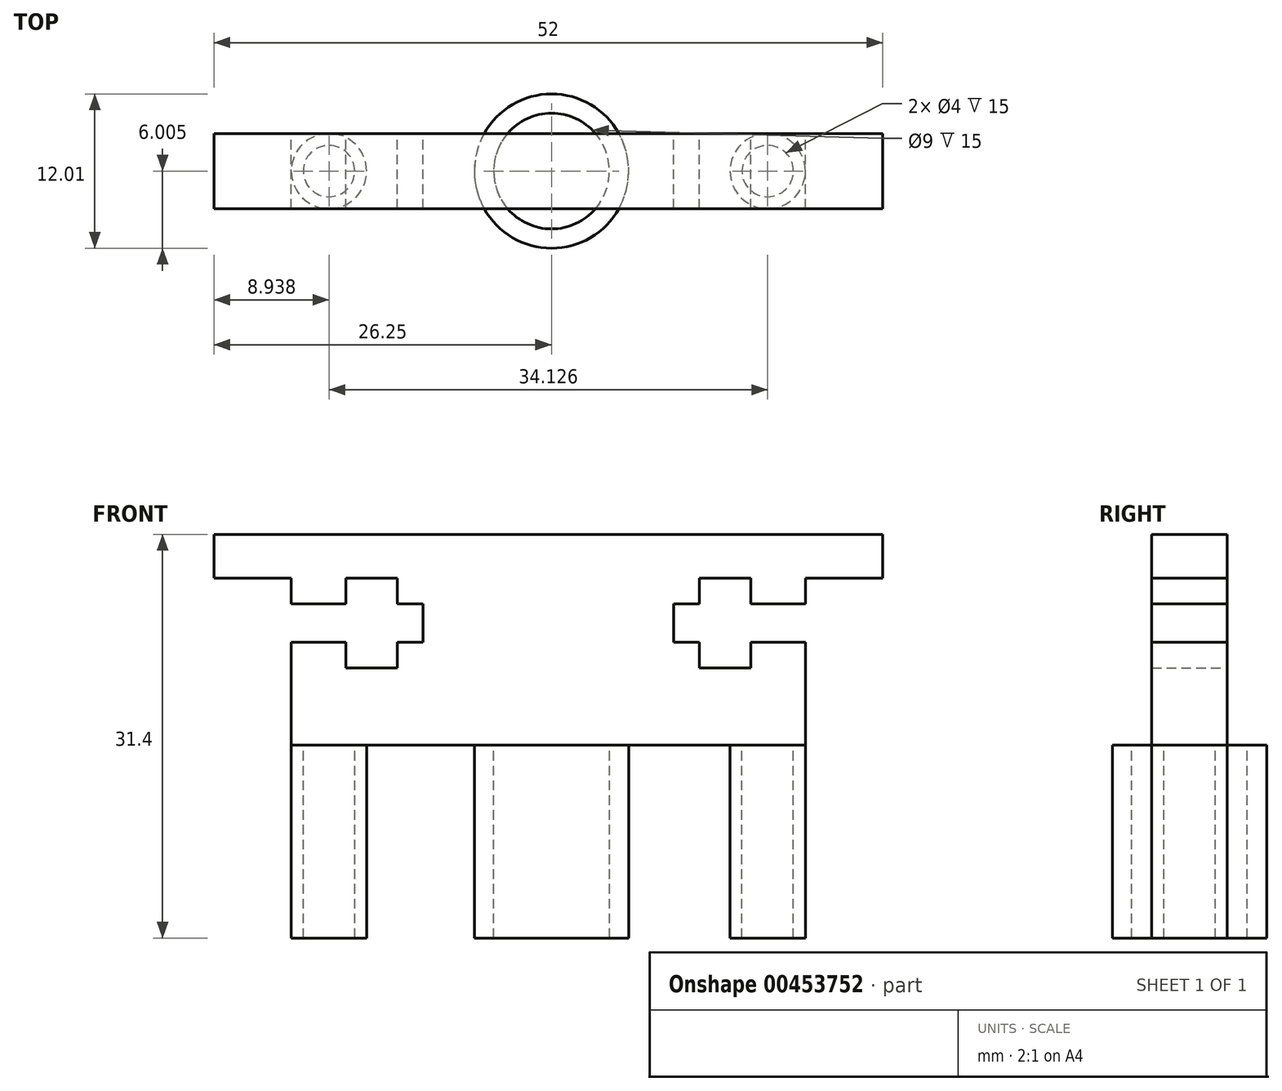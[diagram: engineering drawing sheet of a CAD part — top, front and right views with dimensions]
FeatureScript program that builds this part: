
annotation { "Feature Type Name" : "Feature", "Feature Type Description" : "" }
export const myFeature = defineFeature(function(context is Context, id is Id, definition is map)
    precondition{}
    {
        {
            var Q0;
            Q0=qCreatedBy(makeId("Front.planeOp"),FACE);
            var sketch = newSketch(context, id + "F0", { "sketchPlane" : qUnion([Q0])});
            skLineSegment(sketch, "E0", {"start": v(-19.23, 35.5) * mm, "end": v(-19.23, 32.1) * mm});
            skLineSegment(sketch, "E1", {"start": v(-13.23, 32.1) * mm, "end": v(-19.23, 32.1) * mm});
            skLineSegment(sketch, "E2", {"start": v(-13.23, 32.1) * mm, "end": v(-13.23, 30.1) * mm});
            skLineSegment(sketch, "E3", {"start": v(-13.23, 30.1) * mm, "end": v(-8.98, 30.1) * mm});
            skLineSegment(sketch, "E4", {"start": v(-8.98, 30.1) * mm, "end": v(-8.98, 32.1) * mm});
            skLineSegment(sketch, "E5", {"start": v(-8.98, 32.1) * mm, "end": v(-4.98, 32.1) * mm});
            skLineSegment(sketch, "E6", {"start": v(-4.98, 32.1) * mm, "end": v(-4.98, 30.1) * mm});
            skLineSegment(sketch, "E7", {"start": v(-4.98, 30.1) * mm, "end": v(-2.98, 30.1) * mm});
            skLineSegment(sketch, "E8", {"start": v(-2.98, 30.1) * mm, "end": v(-2.98, 27.1) * mm});
            skLineSegment(sketch, "E9", {"start": v(-2.98, 27.1) * mm, "end": v(-4.98, 27.1) * mm});
            skLineSegment(sketch, "E10", {"start": v(-4.98, 27.1) * mm, "end": v(-4.98, 25.1) * mm});
            skLineSegment(sketch, "E11", {"start": v(-4.98, 25.1) * mm, "end": v(-8.98, 25.1) * mm});
            skLineSegment(sketch, "E12", {"start": v(-8.98, 25.1) * mm, "end": v(-8.98, 27.1) * mm});
            skLineSegment(sketch, "E13", {"start": v(-8.98, 27.1) * mm, "end": v(-13.23, 27.1) * mm});
            skLineSegment(sketch, "E14", {"start": v(-13.23, 27.1) * mm, "end": v(-13.23, 19.1) * mm});
            skLineSegment(sketch, "E15", {"start": v(-19.23, 35.5) * mm, "end": v(6.77, 35.5) * mm});
            skLineSegment(sketch, "E16", {"start": v(-13.23, 19.1) * mm, "end": v(6.77, 19.1) * mm});
            skLineSegment(sketch, "E17", {"start": v(6.77, 19.1) * mm, "end": v(6.77, 35.5) * mm});
            skLineSegment(sketch, "E18.MirrorCS", {"start": v(32.77, 35.5) * mm, "end": v(6.77, 35.5) * mm});
            skLineSegment(sketch, "E19.MirrorCS", {"start": v(32.77, 35.5) * mm, "end": v(32.77, 32.1) * mm});
            skLineSegment(sketch, "E20.MirrorCS", {"start": v(26.77, 32.1) * mm, "end": v(32.77, 32.1) * mm});
            skLineSegment(sketch, "E21.MirrorCS", {"start": v(26.77, 32.1) * mm, "end": v(26.77, 30.1) * mm});
            skLineSegment(sketch, "E22.MirrorCS", {"start": v(26.77, 30.1) * mm, "end": v(22.52, 30.1) * mm});
            skLineSegment(sketch, "E23.MirrorCS", {"start": v(22.52, 32.1) * mm, "end": v(18.52, 32.1) * mm});
            skLineSegment(sketch, "E24.MirrorCS", {"start": v(18.52, 32.1) * mm, "end": v(18.52, 30.1) * mm});
            skLineSegment(sketch, "E25.MirrorCS", {"start": v(22.52, 30.1) * mm, "end": v(22.52, 32.1) * mm});
            skLineSegment(sketch, "E26.MirrorCS", {"start": v(16.52, 30.1) * mm, "end": v(16.52, 27.1) * mm});
            skLineSegment(sketch, "E27.MirrorCS", {"start": v(16.52, 27.1) * mm, "end": v(18.52, 27.1) * mm});
            skLineSegment(sketch, "E28.MirrorCS", {"start": v(18.52, 25.1) * mm, "end": v(22.52, 25.1) * mm});
            skLineSegment(sketch, "E29.MirrorCS", {"start": v(22.52, 25.1) * mm, "end": v(22.52, 27.1) * mm});
            skLineSegment(sketch, "E30.MirrorCS", {"start": v(22.52, 27.1) * mm, "end": v(26.77, 27.1) * mm});
            skLineSegment(sketch, "E31.MirrorCS", {"start": v(26.77, 27.1) * mm, "end": v(26.77, 19.1) * mm});
            skLineSegment(sketch, "E32.MirrorCS", {"start": v(26.77, 19.1) * mm, "end": v(6.77, 19.1) * mm});
            skLineSegment(sketch, "E33.MirrorCS", {"start": v(18.52, 30.1) * mm, "end": v(16.52, 30.1) * mm});
            skLineSegment(sketch, "E34.MirrorCS", {"start": v(18.52, 27.1) * mm, "end": v(18.52, 25.1) * mm});
            skSolve(sketch);
        }
        {
            var Q0;
            Q0=makeQuery(id+"F0.imprint","IMPRINT",FACE,{"disambiguationData":[TD([[makeQuery(id+"F0.imprint","IMPRINT",EDGE,{"derivedFrom":sQuery(id+"F0.wireOp",EDGE,"E0")}),1.0]])]});
            var Q1;
            Q1=makeQuery(id+"F0.imprint","IMPRINT",FACE,{"disambiguationData":[TD([[makeQuery(id+"F0.imprint","IMPRINT",EDGE,{"derivedFrom":sQuery(id+"F0.wireOp",EDGE,"E17")}),-1.0]])]});
            extrude(context, id + "F1", {"entities" : qUnion([Q0, Q1]), "depth" : 5.85 * mm});
        }
        {
            var Q0;
            Q0=makeQuery(id+"F1.opExtrude","SWEPT_FACE",FACE,{"disambiguationData":[OSD([sQuery(id+"F0.wireOp",EDGE,"E16"),sQuery(id+"F0.wireOp",EDGE,"E32.MirrorCS")])]});
            var sketch = newSketch(context, id + "F2", { "sketchPlane" : qUnion([Q0])});
            skCircle(sketch, "E35", {"center": v(-10.3, 2.93) * mm, "radius": 2.93 * mm});
            skPoint(sketch, "E35.centerSnap0", {"position": v(-13.23, 2.93) * mm});
            skCircle(sketch, "E36", {"center": v(-10.3, 2.93) * mm, "radius": 2 * mm});
            skCircle(sketch, "E37.MirrorC", {"center": v(23.83, 2.93) * mm, "radius": 2.93 * mm});
            skCircle(sketch, "E38.MirrorC", {"center": v(23.83, 2.93) * mm, "radius": 2 * mm});
            skPoint(sketch, "E39.centerSnap0", {"position": v(6.77, 5.85) * mm});
            skCircle(sketch, "E40", {"center": v(7.02, 2.93) * mm, "radius": 6 * mm});
            skCircle(sketch, "E41", {"center": v(7.02, 2.93) * mm, "radius": 4.5 * mm});
            skSolve(sketch);
        }
        {
            var Q0;
            Q0 = qSketchRegion(id + "F2", true);
            extrude(context, id + "F3", {"entities" : qUnion([Q0]), "operationType" : NewBodyOperationType.ADD, "depth" : 15 * mm});
        }
    });
